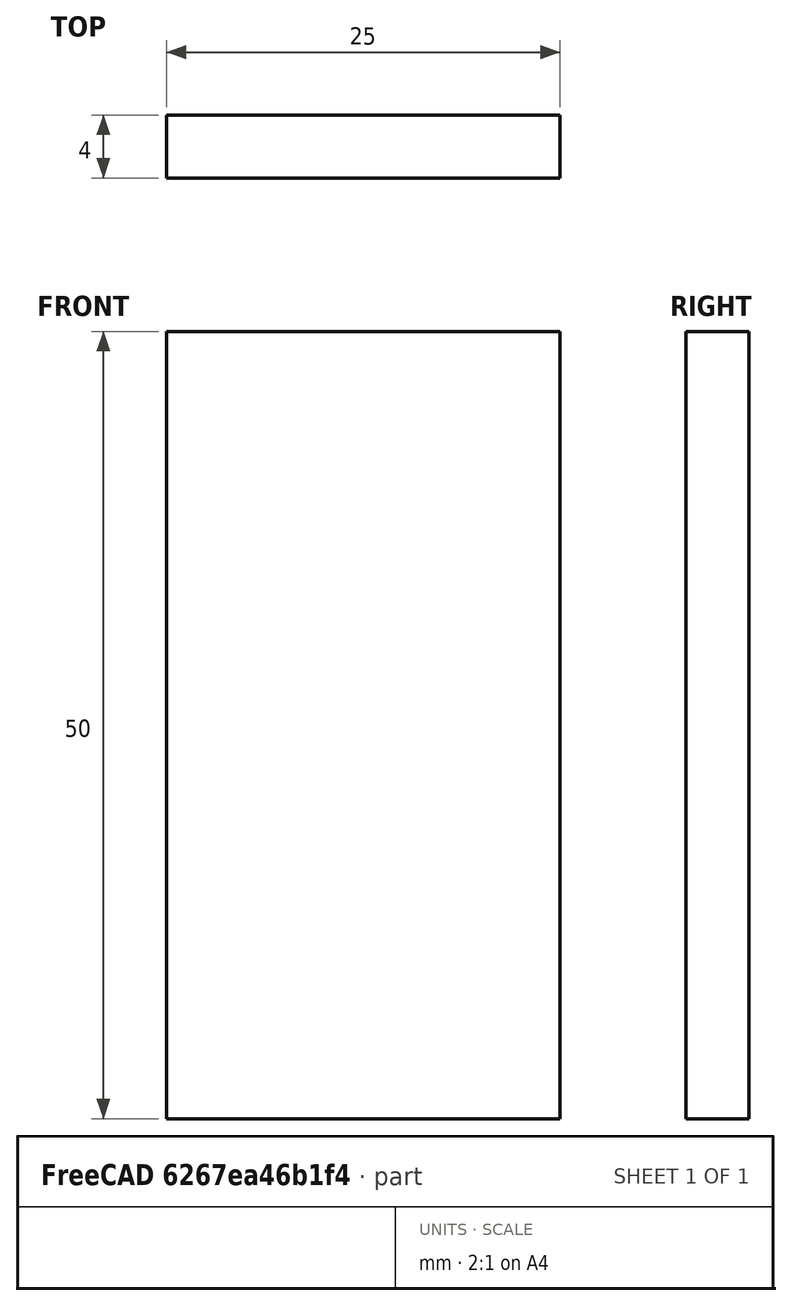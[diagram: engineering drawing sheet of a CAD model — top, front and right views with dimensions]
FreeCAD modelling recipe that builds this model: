
FCSTD DOCUMENT  (FreeCAD 0.15R4671 (Git))
Label: Flat Bar 25x4 EN10058 S235JR
License: All rights reserved
LicenseURL: http://en.wikipedia.org/wiki/All_rights_reserved
objects: Sketcher::SketchObject×1, Part::Extrusion×1
note: 2 computed .brp shape members not serialized (recipe doc carries the construction recipe); baked Part::Feature solids carry a one-line shape summary decoded from their .brp

FEATURE [Sketcher::SketchObject] Sketch
  sketch-geometry (4):
    g0: LineSegment StartX=-12.5 StartY=-2 StartZ=0 EndX=12.5 EndY=-2 EndZ=0
    g1: LineSegment StartX=12.5 StartY=-2 StartZ=0 EndX=12.5 EndY=2 EndZ=0
    g2: LineSegment StartX=12.5 StartY=2 StartZ=0 EndX=-12.5 EndY=2 EndZ=0
    g3: LineSegment StartX=-12.5 StartY=2 StartZ=0 EndX=-12.5 EndY=-2 EndZ=0
  constraints (12):
    c: Coincident(g0,g1)
    c: Coincident(g1,g2)
    c: Coincident(g2,g3)
    c: Coincident(g3,g0)
    c: Horizontal(g0)
    c: Horizontal(g2)
    c: Vertical(g1)
    c: Vertical(g3)
    c: Symmetric(g1,g2,g-2)
    c: Symmetric(g0,g1,g-1)
    c: DistanceY(g1) = 4
    c: DistanceX(g0) = 25
FEATURE [Part::Extrusion] Extrude  label="Flat Bar 25x4 EN10058 S235JR"
  Base = -> Sketch
  Dir = (0,0,50)
  Solid = true
